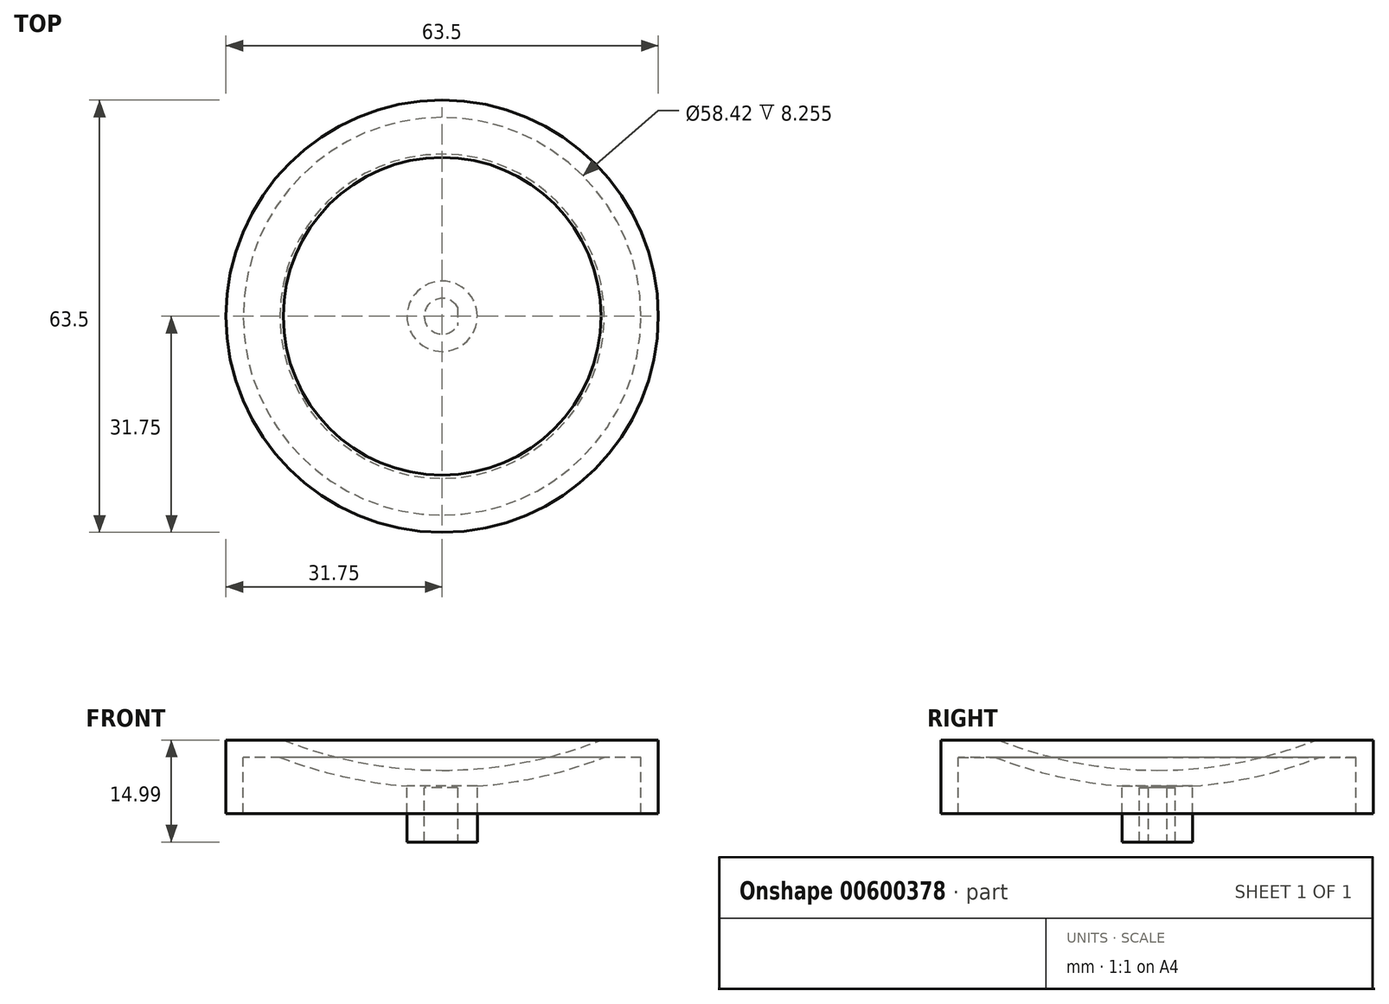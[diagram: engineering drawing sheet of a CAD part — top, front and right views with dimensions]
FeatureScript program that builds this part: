
annotation { "Feature Type Name" : "Feature", "Feature Type Description" : "" }
export const myFeature = defineFeature(function(context is Context, id is Id, definition is map)
    precondition{}
    {
        {
            var Q0;
            Q0=qCreatedBy(makeId("Front.planeOp"),FACE);
            var sketch = newSketch(context, id + "F0", { "sketchPlane" : qUnion([Q0])});
            skCircle(sketch, "E0", {"center": v(0, 59.06) * mm, "radius": 63.5 * mm, "construction": true});
            skLineSegment(sketch, "E1", {"start": v(0, -4.44) * mm, "end": v(0, -6.98) * mm});
            skLineSegment(sketch, "E2", {"start": v(0, -6.98) * mm, "end": v(2.62, -6.98) * mm});
            skLineSegment(sketch, "E3", {"start": v(2.62, -6.98) * mm, "end": v(2.63, -14.98) * mm});
            skLineSegment(sketch, "E4", {"start": v(2.63, -14.98) * mm, "end": v(5.17, -14.98) * mm});
            skLineSegment(sketch, "E5", {"start": v(5.17, -14.98) * mm, "end": v(5.17, -6.78) * mm});
            skLineSegment(sketch, "E6", {"start": v(23.34, 0) * mm, "end": v(31.75, 0) * mm});
            skLineSegment(sketch, "E7", {"start": v(31.75, 0) * mm, "end": v(31.75, -10.8) * mm});
            skLineSegment(sketch, "E8", {"start": v(31.75, -10.8) * mm, "end": v(29.21, -10.8) * mm});
            skLineSegment(sketch, "E9", {"start": v(29.21, -10.8) * mm, "end": v(29.21, -2.54) * mm});
            skLineSegment(sketch, "E10", {"start": v(29.21, -2.54) * mm, "end": v(23.82, -2.54) * mm});
            skArc(sketch, "E11", {"start": v(0, -4.44) * mm, "mid": v(11.88, -3.32) * mm, "end": v(23.34, 0) * mm});
            skArc(sketch, "E12", {"start": v(5.17, -6.78) * mm, "mid": v(14.65, -5.34) * mm, "end": v(23.82, -2.54) * mm});
            skSolve(sketch);
        }
        {
            var Q0;
            Q0=makeQuery(id+"F0.imprint","IMPRINT",FACE,{"disambiguationData":[TD([[makeQuery(id+"F0.imprint","IMPRINT",EDGE,{"derivedFrom":sQuery(id+"F0.wireOp",EDGE,"E1")}),1.0]])]});
            var Q1;
            Q1=sQuery(id+"F0.wireOp",EDGE,"E1");
            revolve(context, id + "F1", {"entities" : qUnion([Q0]), "axis" : qUnion([Q1]), "revolveType" : RevolveType.FULL});
        }
        {
            var Q0;
            Q0=makeQuery(id+"F1.opRevolve","SWEPT_FACE",FACE,{"disambiguationData":[OSD([sQuery(id+"F0.wireOp",EDGE,"E4")])]});
            var sketch = newSketch(context, id + "F2", { "sketchPlane" : qUnion([Q0])});
            skCircle(sketch, "E13.0.0", {"center": v(0, 0) * mm, "radius": 2.63 * mm});
            skLineSegment(sketch, "E14", {"start": v(2.25, -1.35) * mm, "end": v(2.25, 1.35) * mm});
            skSolve(sketch);
        }
        {
            var Q0;
            {var subQ0=sQuery(id+"F2.wireOp",EDGE,"E14");Q0=makeQuery(id+"F2.imprint","IMPRINT",FACE,{"disambiguationData":[TD([[makeQuery(id+"F2.imprint","IMPRINT",EDGE,{"derivedFrom":subQ0}),-1.0]])]});}
            extrude(context, id + "F3", {"entities" : qUnion([Q0]), "operationType" : NewBodyOperationType.ADD, "oppositeDirection" : true, "depth" : 8 * mm, "offsetDistance" : 25.4 * mm});
        }
    });
